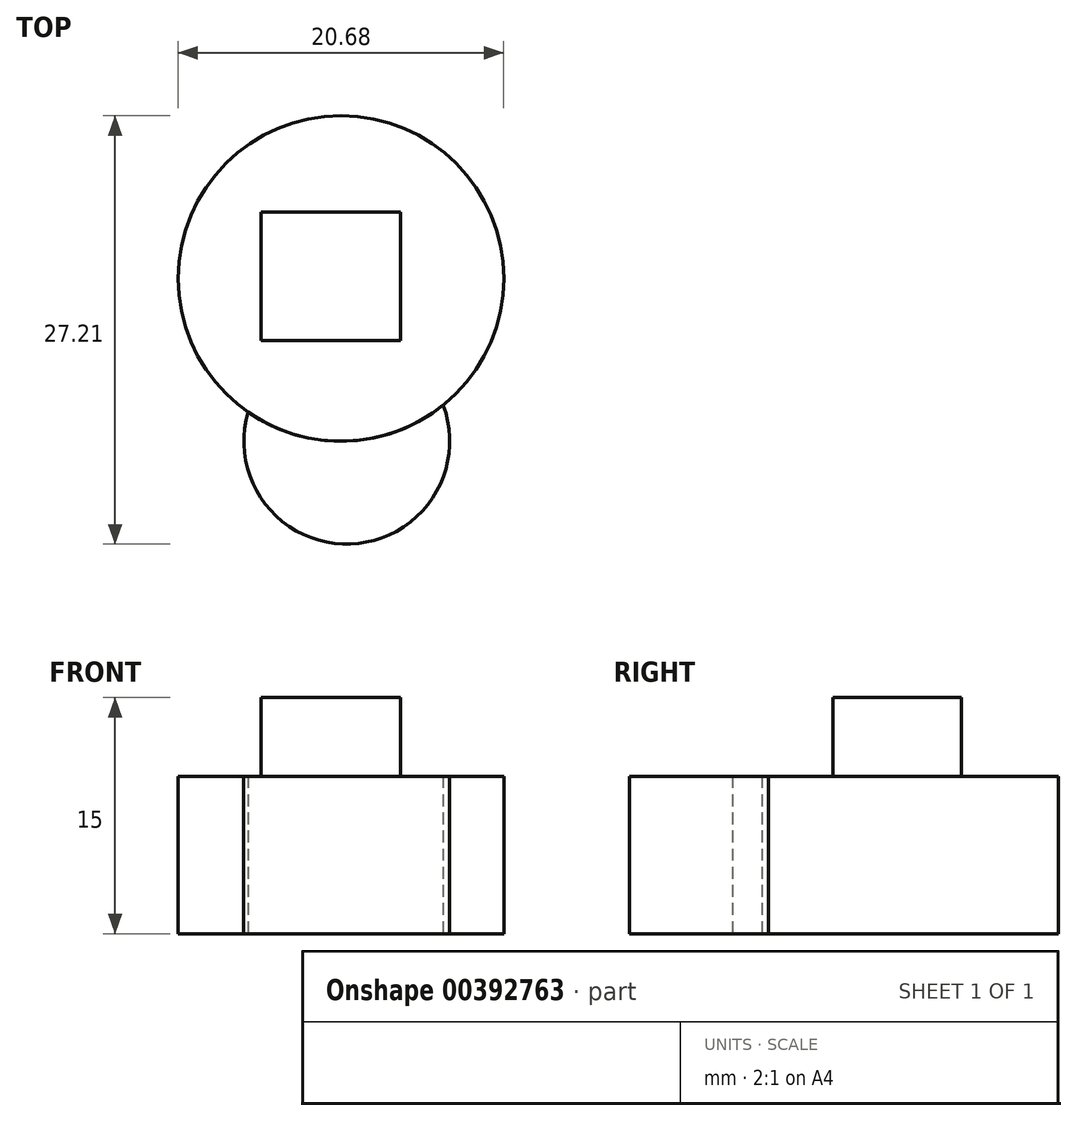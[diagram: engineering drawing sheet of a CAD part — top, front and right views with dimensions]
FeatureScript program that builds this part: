
annotation { "Feature Type Name" : "Feature", "Feature Type Description" : "" }
export const myFeature = defineFeature(function(context is Context, id is Id, definition is map)
    precondition{}
    {
        {
            var Q0;
            Q0=qCreatedBy(makeId("Top.planeOp"),FACE);
            var sketch = newSketch(context, id + "F0", { "sketchPlane" : qUnion([Q0])});
            skCircle(sketch, "E0", {"center": v(-36.56, -21.1) * mm, "radius": 10.34 * mm});
            skSolve(sketch);
        }
        {
            var Q0;
            Q0=makeQuery(id+"F0.imprint","IMPRINT",FACE,{"disambiguationData":[TD([[makeQuery(id+"F0.imprint","IMPRINT",EDGE,{"derivedFrom":sQuery(id+"F0.wireOp",EDGE,"E0")}),1.0]])]});
            extrude(context, id + "F1", {"entities" : qUnion([Q0]), "depth" : 10 * mm});
        }
        {
            var Q0;
            Q0=makeQuery(id+"F1.opExtrude","CAP_FACE",FACE,{"disambiguationData":[OSD([sQuery(id+"F0.wireOp",EDGE,"E0")])],"isStart":false});
            var sketch = newSketch(context, id + "F2", { "sketchPlane" : qUnion([Q0])});
            skLineSegment(sketch, "E1.bottom", {"start": v(-41.63, -16.9) * mm, "end": v(-32.78, -16.9) * mm});
            skLineSegment(sketch, "E1.top", {"start": v(-41.63, -25.06) * mm, "end": v(-32.78, -25.06) * mm});
            skLineSegment(sketch, "E1.left", {"start": v(-41.63, -16.9) * mm, "end": v(-41.63, -25.06) * mm});
            skLineSegment(sketch, "E1.right", {"start": v(-32.78, -16.9) * mm, "end": v(-32.78, -25.06) * mm});
            skSolve(sketch);
        }
        {
            var Q0;
            Q0=makeQuery(id+"F2.imprint","IMPRINT",FACE,{"disambiguationData":[TD([[makeQuery(id+"F2.imprint","IMPRINT",EDGE,{"derivedFrom":sQuery(id+"F2.wireOp",EDGE,"E1.bottom")}),-1.0]])]});
            extrude(context, id + "F3", {"entities" : qUnion([Q0]), "depth" : 5 * mm});
        }
        {
            var Q0;
            Q0=makeQuery(id+"F1.opExtrude","CAP_FACE",FACE,{"disambiguationData":[OSD([sQuery(id+"F0.wireOp",EDGE,"E0")])],"isStart":true});
            var sketch = newSketch(context, id + "F4", { "sketchPlane" : qUnion([Q0])});
            skCircle(sketch, "E2", {"center": v(-36.2, 31.44) * mm, "radius": 6.54 * mm});
            skSolve(sketch);
        }
        {
            var Q0;
            {var subQ0=sQuery(id+"F4.wireOp",EDGE,"E2");var subQ1=makeQuery(id+"F1.opExtrude","CAP_EDGE",EDGE,{"disambiguationData":[OSD([sQuery(id+"F0.wireOp",EDGE,"E0")])],"isStart":true});var subQ2=makeQuery(id+"F4.imprint","INTERSECT",VERTEX,{"disambiguationData":[OD(0.0)],"derivedFrom":[subQ1,subQ0]});Q0=makeQuery(id+"F4.imprint","IMPRINT",FACE,{"disambiguationData":[TD([[makeQuery(id+"F4.imprint","IMPRINT",EDGE,{"disambiguationData":[TD([[subQ2,1.0]])],"derivedFrom":subQ0}),1.0]])]});}
            extrude(context, id + "F5", {"entities" : qUnion([Q0]), "oppositeDirection" : true, "depth" : 10 * mm});
        }
    });
